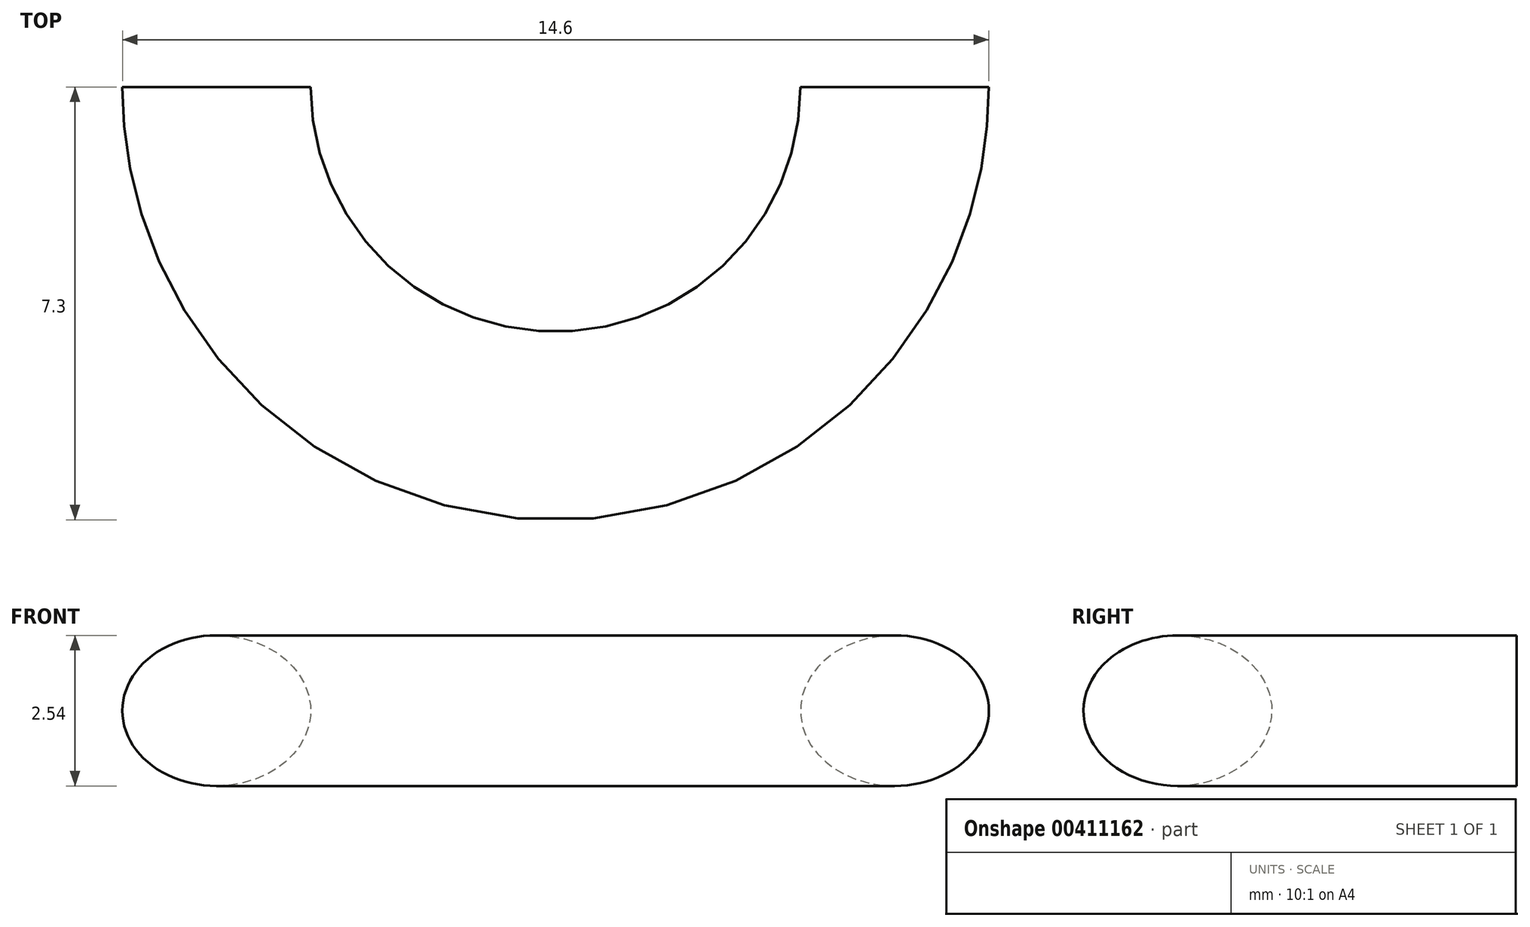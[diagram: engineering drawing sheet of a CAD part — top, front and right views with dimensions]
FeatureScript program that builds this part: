
annotation { "Feature Type Name" : "Feature", "Feature Type Description" : "" }
export const myFeature = defineFeature(function(context is Context, id is Id, definition is map)
    precondition{}
    {
        {
            var Q0;
            Q0=qCreatedBy(makeId("Front.planeOp"),FACE);
            var sketch = newSketch(context, id + "F0", { "sketchPlane" : qUnion([Q0])});
            skEllipse(sketch, "E0", {"center": v(5.72, 0) * mm, "majorRadius": 1.59 * mm, "minorRadius": 1.27 * mm, "majorAxis": v(1, 0)});
            skLineSegment(sketch, "E1", {"start": v(5.72, 0) * mm, "end": v(0, 0) * mm});
            skSolve(sketch);
        }
        {
            var Q0;
            Q0=qCreatedBy(makeId("Right.planeOp"),FACE);
            var sketch = newSketch(context, id + "F1", { "sketchPlane" : qUnion([Q0])});
            skLineSegment(sketch, "E2", {"start": v(0, 0) * mm, "end": v(-6.35, 0) * mm});
            skSolve(sketch);
        }
        {
            var Q0;
            Q0=qCreatedBy(makeId("Front.planeOp"),FACE);
            var sketch = newSketch(context, id + "F2", { "sketchPlane" : qUnion([Q0])});
            skLineSegment(sketch, "E3", {"start": v(0, -2.86) * mm, "end": v(0, 2.86) * mm});
            skSolve(sketch);
        }
        {
            var Q0;
            Q0=makeQuery(id+"F0.imprint","IMPRINT",FACE,{"disambiguationData":[TD([[makeQuery(id+"F0.imprint","IMPRINT",EDGE,{"derivedFrom":sQuery(id+"F0.wireOp",EDGE,"E0")}),1.0]])]});
            var Q1;
            Q1=sQuery(id+"F2.wireOp",EDGE,"E3");
            revolve(context, id + "F3", {"entities" : qUnion([Q0]), "axis" : qUnion([Q1]), "revolveType" : RevolveType.ONE_DIRECTION, "oppositeDirection" : true, "angle" : 180 * degree});
        }
    });
